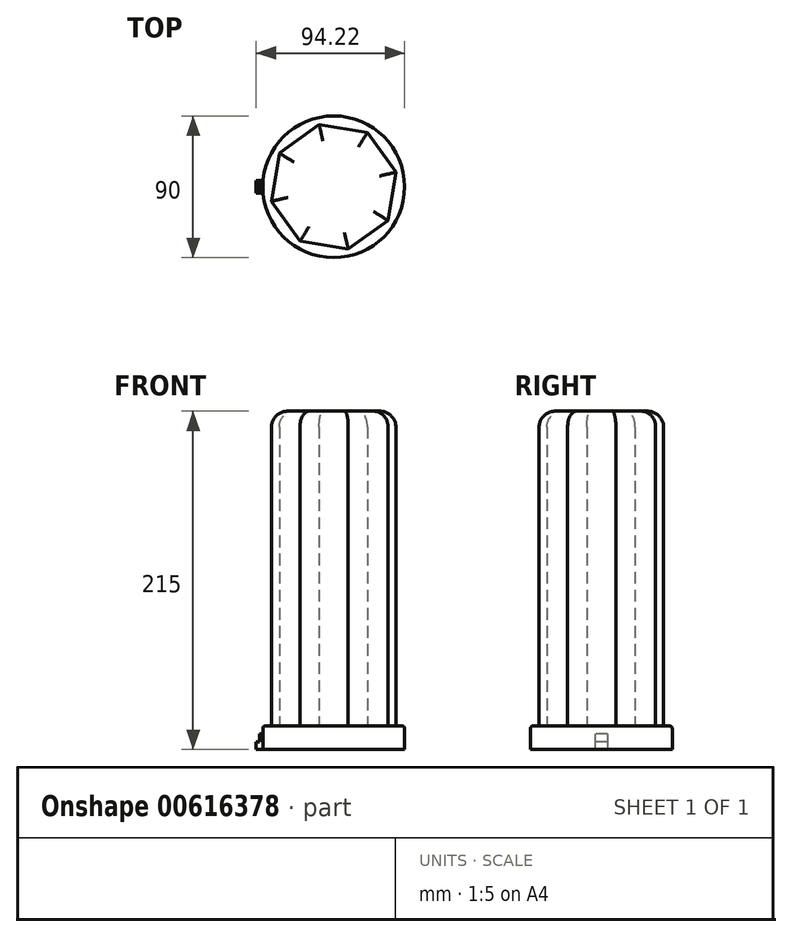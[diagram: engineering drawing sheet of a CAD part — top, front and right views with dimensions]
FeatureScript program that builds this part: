
annotation { "Feature Type Name" : "Feature", "Feature Type Description" : "" }
export const myFeature = defineFeature(function(context is Context, id is Id, definition is map)
    precondition{}
    {
        {
            var Q0;
            Q0=qCreatedBy(makeId("Top.planeOp"),FACE);
            var sketch = newSketch(context, id + "F0", { "sketchPlane" : qUnion([Q0])});
            skCircle(sketch, "E0", {"center": v(0, 0) * mm, "radius": 45 * mm});
            skSolve(sketch);
        }
        {
            var Q0;
            Q0=makeQuery(id+"F0.imprint","IMPRINT",FACE,{"disambiguationData":[TD([[makeQuery(id+"F0.imprint","IMPRINT",EDGE,{"derivedFrom":sQuery(id+"F0.wireOp",EDGE,"E0")}),1.0]])]});
            extrude(context, id + "F1", {"entities" : qUnion([Q0]), "depth" : 15 * mm, "offsetDistance" : 25 * mm});
        }
        {
            var Q0;
            Q0=makeQuery(id+"F1.opExtrude","CAP_FACE",FACE,{"disambiguationData":[OSD([sQuery(id+"F0.wireOp",EDGE,"E0")])],"isStart":false});
            var sketch = newSketch(context, id + "F2", { "sketchPlane" : qUnion([Q0])});
            skCircle(sketch, "E1", {"center": v(0, 0) * mm, "radius": 37.5 * mm});
            skCircle(sketch, "E2.cCircle", {"center": v(0, 0) * mm, "radius": 37.5 * mm, "construction": true});
            skLineSegment(sketch, "E2.0", {"start": v(34.48, -21.41) * mm, "end": v(9.24, -39.52) * mm});
            skLineSegment(sketch, "E2.1", {"start": v(9.24, -39.52) * mm, "end": v(-21.41, -34.48) * mm});
            skLineSegment(sketch, "E2.2", {"start": v(-21.41, -34.48) * mm, "end": v(-39.52, -9.24) * mm});
            skLineSegment(sketch, "E2.3", {"start": v(-39.52, -9.24) * mm, "end": v(-34.48, 21.41) * mm});
            skLineSegment(sketch, "E2.4", {"start": v(-34.48, 21.41) * mm, "end": v(-9.24, 39.52) * mm});
            skLineSegment(sketch, "E2.5", {"start": v(-9.24, 39.52) * mm, "end": v(21.41, 34.48) * mm});
            skLineSegment(sketch, "E2.6", {"start": v(21.41, 34.48) * mm, "end": v(39.52, 9.24) * mm});
            skLineSegment(sketch, "E2.7", {"start": v(39.52, 9.24) * mm, "end": v(34.48, -21.41) * mm});
            skPoint(sketch, "E2.0.midPoint", {"position": v(21.86, -30.47) * mm});
            skSolve(sketch);
        }
        {
            var Q0;
            {var subQ0=sQuery(id+"F2.wireOp",EDGE,"E2.4");var subQ1=sQuery(id+"F2.wireOp",EDGE,"E1");var subQ2=makeQuery(id+"F2.imprint","INTERSECT",VERTEX,{"derivedFrom":[subQ1,subQ0]});Q0=makeQuery(id+"F2.imprint","IMPRINT",FACE,{"disambiguationData":[TD([[makeQuery(id+"F2.imprint","IMPRINT",EDGE,{"disambiguationData":[TD([[subQ2,-1.0]])],"derivedFrom":subQ1}),-1.0]])]});}
            var Q1;
            {var subQ0=sQuery(id+"F2.wireOp",EDGE,"E2.5");var subQ1=sQuery(id+"F2.wireOp",EDGE,"E1");var subQ2=makeQuery(id+"F2.imprint","INTERSECT",VERTEX,{"derivedFrom":[subQ1,subQ0]});Q1=makeQuery(id+"F2.imprint","IMPRINT",FACE,{"disambiguationData":[TD([[makeQuery(id+"F2.imprint","IMPRINT",EDGE,{"disambiguationData":[TD([[subQ2,-1.0]])],"derivedFrom":subQ1}),-1.0]])]});}
            var Q2;
            {var subQ0=sQuery(id+"F2.wireOp",EDGE,"E2.5");var subQ1=sQuery(id+"F2.wireOp",EDGE,"E1");var subQ2=makeQuery(id+"F2.imprint","INTERSECT",VERTEX,{"derivedFrom":[subQ1,subQ0]});Q2=makeQuery(id+"F2.imprint","IMPRINT",FACE,{"disambiguationData":[TD([[makeQuery(id+"F2.imprint","IMPRINT",EDGE,{"disambiguationData":[TD([[subQ2,1.0]])],"derivedFrom":subQ1}),-1.0]])]});}
            var Q3;
            {var subQ0=sQuery(id+"F2.wireOp",EDGE,"E2.6");var subQ1=sQuery(id+"F2.wireOp",EDGE,"E1");var subQ2=makeQuery(id+"F2.imprint","INTERSECT",VERTEX,{"derivedFrom":[subQ1,subQ0]});Q3=makeQuery(id+"F2.imprint","IMPRINT",FACE,{"disambiguationData":[TD([[makeQuery(id+"F2.imprint","IMPRINT",EDGE,{"disambiguationData":[TD([[subQ2,1.0]])],"derivedFrom":subQ1}),-1.0]])]});}
            var Q4;
            {var subQ0=sQuery(id+"F2.wireOp",EDGE,"E2.3");var subQ1=sQuery(id+"F2.wireOp",EDGE,"E1");var subQ2=makeQuery(id+"F2.imprint","INTERSECT",VERTEX,{"derivedFrom":[subQ1,subQ0]});Q4=makeQuery(id+"F2.imprint","IMPRINT",FACE,{"disambiguationData":[TD([[makeQuery(id+"F2.imprint","IMPRINT",EDGE,{"disambiguationData":[TD([[subQ2,-1.0]])],"derivedFrom":subQ1}),-1.0]])]});}
            var Q5;
            {var subQ0=sQuery(id+"F2.wireOp",EDGE,"E2.2");var subQ1=sQuery(id+"F2.wireOp",EDGE,"E1");var subQ2=makeQuery(id+"F2.imprint","INTERSECT",VERTEX,{"derivedFrom":[subQ1,subQ0]});Q5=makeQuery(id+"F2.imprint","IMPRINT",FACE,{"disambiguationData":[TD([[makeQuery(id+"F2.imprint","IMPRINT",EDGE,{"disambiguationData":[TD([[subQ2,-1.0]])],"derivedFrom":subQ1}),-1.0]])]});}
            var Q6;
            {var subQ0=sQuery(id+"F2.wireOp",EDGE,"E2.1");var subQ1=sQuery(id+"F2.wireOp",EDGE,"E1");var subQ2=makeQuery(id+"F2.imprint","INTERSECT",VERTEX,{"derivedFrom":[subQ1,subQ0]});Q6=makeQuery(id+"F2.imprint","IMPRINT",FACE,{"disambiguationData":[TD([[makeQuery(id+"F2.imprint","IMPRINT",EDGE,{"disambiguationData":[TD([[subQ2,-1.0]])],"derivedFrom":subQ1}),-1.0]])]});}
            var Q7;
            {var subQ0=sQuery(id+"F2.wireOp",EDGE,"E2.0");var subQ1=sQuery(id+"F2.wireOp",EDGE,"E1");var subQ2=makeQuery(id+"F2.imprint","INTERSECT",VERTEX,{"derivedFrom":[subQ1,subQ0]});Q7=makeQuery(id+"F2.imprint","IMPRINT",FACE,{"disambiguationData":[TD([[makeQuery(id+"F2.imprint","IMPRINT",EDGE,{"disambiguationData":[TD([[subQ2,-1.0]])],"derivedFrom":subQ1}),-1.0]])]});}
            var Q8;
            {var subQ0=sQuery(id+"F2.wireOp",EDGE,"E1");var subQ4=makeQuery(id+"F2.imprint","INTERSECT",VERTEX,{"derivedFrom":[subQ0,sQuery(id+"F2.wireOp",EDGE,"E2.5")]});Q8=makeQuery(id+"F2.imprint","IMPRINT",FACE,{"disambiguationData":[TD([[makeQuery(id+"F2.imprint","IMPRINT",EDGE,{"disambiguationData":[TD([[subQ4,1.0]])],"derivedFrom":subQ0}),1.0]])]});}
            extrude(context, id + "F3", {"entities" : qUnion([Q0, Q1, Q2, Q3, Q4, Q5, Q6, Q7, Q8]), "operationType" : NewBodyOperationType.ADD, "depth" : 200 * mm, "offsetDistance" : 25 * mm});
        }
        {
            var Q0;
            Q0=makeQuery(id+"F3.opExtrude","CAP_FACE",FACE,{"disambiguationData":[OSD([sQuery(id+"F2.wireOp",EDGE,"E2.0"),sQuery(id+"F2.wireOp",EDGE,"E2.1"),sQuery(id+"F2.wireOp",EDGE,"E2.2"),sQuery(id+"F2.wireOp",EDGE,"E2.3"),sQuery(id+"F2.wireOp",EDGE,"E2.4"),sQuery(id+"F2.wireOp",EDGE,"E2.5"),sQuery(id+"F2.wireOp",EDGE,"E2.6"),sQuery(id+"F2.wireOp",EDGE,"E2.7")])],"isStart":false});
            var sketch = newSketch(context, id + "F4", { "sketchPlane" : qUnion([Q0])});
            skCircle(sketch, "E3", {"center": v(0, 0) * mm, "radius": 45 * mm});
            skSolve(sketch);
        }
        {
            var Q0;
            Q0=makeQuery(id+"F19PEvhqMDMhHkI_1.opExtrude","CAP_EDGE",EDGE,{"disambiguationData":[OSD([sQuery(id+"F4.wireOp",EDGE,"E3")])],"isStart":false});
            var Q1;
            Q1=makeQuery(id+"F1.opExtrude","CAP_EDGE",EDGE,{"disambiguationData":[OSD([sQuery(id+"F0.wireOp",EDGE,"E0")])],"isStart":false});
            fillet(context, id + "F5", {"entities" : qUnion([Q0, Q1]), "radius" : 1.5 * mm, "tangentPropagation" : true, "allowEdgeOverflow" : false});
        }
        {
            var Q0;
            Q0=makeQuery(id+"F1.opExtrude","CAP_FACE",FACE,{"disambiguationData":[OSD([sQuery(id+"F0.wireOp",EDGE,"E0")])],"isStart":true});
            var sketch = newSketch(context, id + "F6", { "sketchPlane" : qUnion([Q0])});
            skLineSegment(sketch, "E4.bottom", {"start": v(0, 0) * mm, "end": v(-35.22, 0) * mm});
            skLineSegment(sketch, "E4.top", {"start": v(0, 4) * mm, "end": v(-35.22, 4) * mm});
            skLineSegment(sketch, "E4.left", {"start": v(0, 0) * mm, "end": v(0, 4) * mm});
            skLineSegment(sketch, "E4.right", {"start": v(-35.22, 0) * mm, "end": v(-35.22, 4) * mm});
            skLineSegment(sketch, "E5.top", {"start": v(0, -4) * mm, "end": v(-35.22, -4) * mm});
            skLineSegment(sketch, "E5.left", {"start": v(0, 0) * mm, "end": v(0, -4) * mm});
            skLineSegment(sketch, "E5.right", {"start": v(-35.22, 0) * mm, "end": v(-35.22, -4) * mm});
            skLineSegment(sketch, "E6.bottom", {"start": v(-35.22, -4) * mm, "end": v(-47.22, -4) * mm});
            skLineSegment(sketch, "E6.top", {"start": v(-35.22, 4) * mm, "end": v(-47.22, 4) * mm});
            skLineSegment(sketch, "E6.left", {"start": v(-35.22, -4) * mm, "end": v(-35.22, 4) * mm});
            skLineSegment(sketch, "E6.right", {"start": v(-47.22, -4) * mm, "end": v(-47.22, 4) * mm});
            skSolve(sketch);
        }
        {
            var Q0;
            {var subQ0=sQuery(id+"F6.wireOp",EDGE,"E6.right");Q0=makeQuery(id+"F6.imprint","IMPRINT",FACE,{"disambiguationData":[TD([[makeQuery(id+"F6.imprint","IMPRINT",EDGE,{"derivedFrom":subQ0}),-1.0]])]});}
            extrude(context, id + "F7", {"entities" : qUnion([Q0]), "oppositeDirection" : true, "depth" : 10 * mm, "offsetDistance" : 25 * mm});
        }
        {
            var Q0;
            Q0=makeQuery(id+"F7.opExtrude","SWEPT_FACE",FACE,{"disambiguationData":[OSD([sQuery(id+"F6.wireOp",EDGE,"E6.right")])]});
            var sketch = newSketch(context, id + "F8", { "sketchPlane" : qUnion([Q0])});
            skLineSegment(sketch, "E7", {"start": v(0, 10) * mm, "end": v(0, 0) * mm});
            skLineSegment(sketch, "E8", {"start": v(0, 0) * mm, "end": v(-4, 0) * mm});
            skLineSegment(sketch, "E9", {"start": v(-4, 0) * mm, "end": v(-4, 5) * mm});
            skLineSegment(sketch, "E10", {"start": v(-4, 5) * mm, "end": v(4, 5) * mm});
            skLineSegment(sketch, "E11", {"start": v(4, 5) * mm, "end": v(4, 0) * mm});
            skLineSegment(sketch, "E12", {"start": v(4, 0) * mm, "end": v(0, 0) * mm});
            skCircle(sketch, "E13", {"center": v(0, 5) * mm, "radius": 1.5 * mm});
            skSolve(sketch);
        }
        {
            var Q0;
            {var subQ0=sQuery(id+"F8.wireOp",EDGE,"E13");var subQ1=sQuery(id+"F8.wireOp",EDGE,"E7");var subQ2=makeQuery(id+"F8.imprint","INTERSECT",VERTEX,{"disambiguationData":[OD(0.0)],"derivedFrom":[subQ1,subQ0]});Q0=makeQuery(id+"F8.imprint","IMPRINT",FACE,{"disambiguationData":[TD([[makeQuery(id+"F8.imprint","IMPRINT",EDGE,{"disambiguationData":[TD([[subQ2,-1.0]])],"derivedFrom":subQ1}),-1.0]])]});}
            var Q1;
            {var subQ0=sQuery(id+"F8.wireOp",EDGE,"E13");var subQ1=sQuery(id+"F8.wireOp",EDGE,"E7");var subQ2=makeQuery(id+"F8.imprint","INTERSECT",VERTEX,{"disambiguationData":[OD(0.0)],"derivedFrom":[subQ1,subQ0]});Q1=makeQuery(id+"F8.imprint","IMPRINT",FACE,{"disambiguationData":[TD([[makeQuery(id+"F8.imprint","IMPRINT",EDGE,{"disambiguationData":[TD([[subQ2,-1.0]])],"derivedFrom":subQ1}),1.0]])]});}
            var Q2;
            {var subQ0=sQuery(id+"F8.wireOp",EDGE,"E10");var subQ1=sQuery(id+"F8.wireOp",EDGE,"E7");var subQ2=makeQuery(id+"F8.imprint","INTERSECT",VERTEX,{"derivedFrom":[subQ1,subQ0]});Q2=makeQuery(id+"F8.imprint","IMPRINT",FACE,{"disambiguationData":[TD([[makeQuery(id+"F8.imprint","IMPRINT",EDGE,{"disambiguationData":[TD([[subQ2,-1.0]])],"derivedFrom":subQ1}),1.0]])]});}
            var Q3;
            {var subQ0=sQuery(id+"F8.wireOp",EDGE,"E10");var subQ1=sQuery(id+"F8.wireOp",EDGE,"E7");var subQ2=makeQuery(id+"F8.imprint","INTERSECT",VERTEX,{"derivedFrom":[subQ1,subQ0]});Q3=makeQuery(id+"F8.imprint","IMPRINT",FACE,{"disambiguationData":[TD([[makeQuery(id+"F8.imprint","IMPRINT",EDGE,{"disambiguationData":[TD([[subQ2,-1.0]])],"derivedFrom":subQ1}),-1.0]])]});}
            extrude(context, id + "F9", {"entities" : qUnion([Q0, Q1, Q2, Q3]), "operationType" : NewBodyOperationType.ADD, "depth" : 2 * mm, "offsetDistance" : 25 * mm});
        }
        {
            var Q0;
            Q0=makeQuery(id+"F3.opExtrude","CAP_FACE",FACE,{"disambiguationData":[OSD([sQuery(id+"F2.wireOp",EDGE,"E2.0"),sQuery(id+"F2.wireOp",EDGE,"E2.1"),sQuery(id+"F2.wireOp",EDGE,"E2.2"),sQuery(id+"F2.wireOp",EDGE,"E2.3"),sQuery(id+"F2.wireOp",EDGE,"E2.4"),sQuery(id+"F2.wireOp",EDGE,"E2.5"),sQuery(id+"F2.wireOp",EDGE,"E2.6"),sQuery(id+"F2.wireOp",EDGE,"E2.7")])],"isStart":false});
            fillet(context, id + "F10", {"entities" : qUnion([Q0]), "radius" : 10 * mm, "tangentPropagation" : true, "allowEdgeOverflow" : false});
        }
    });
